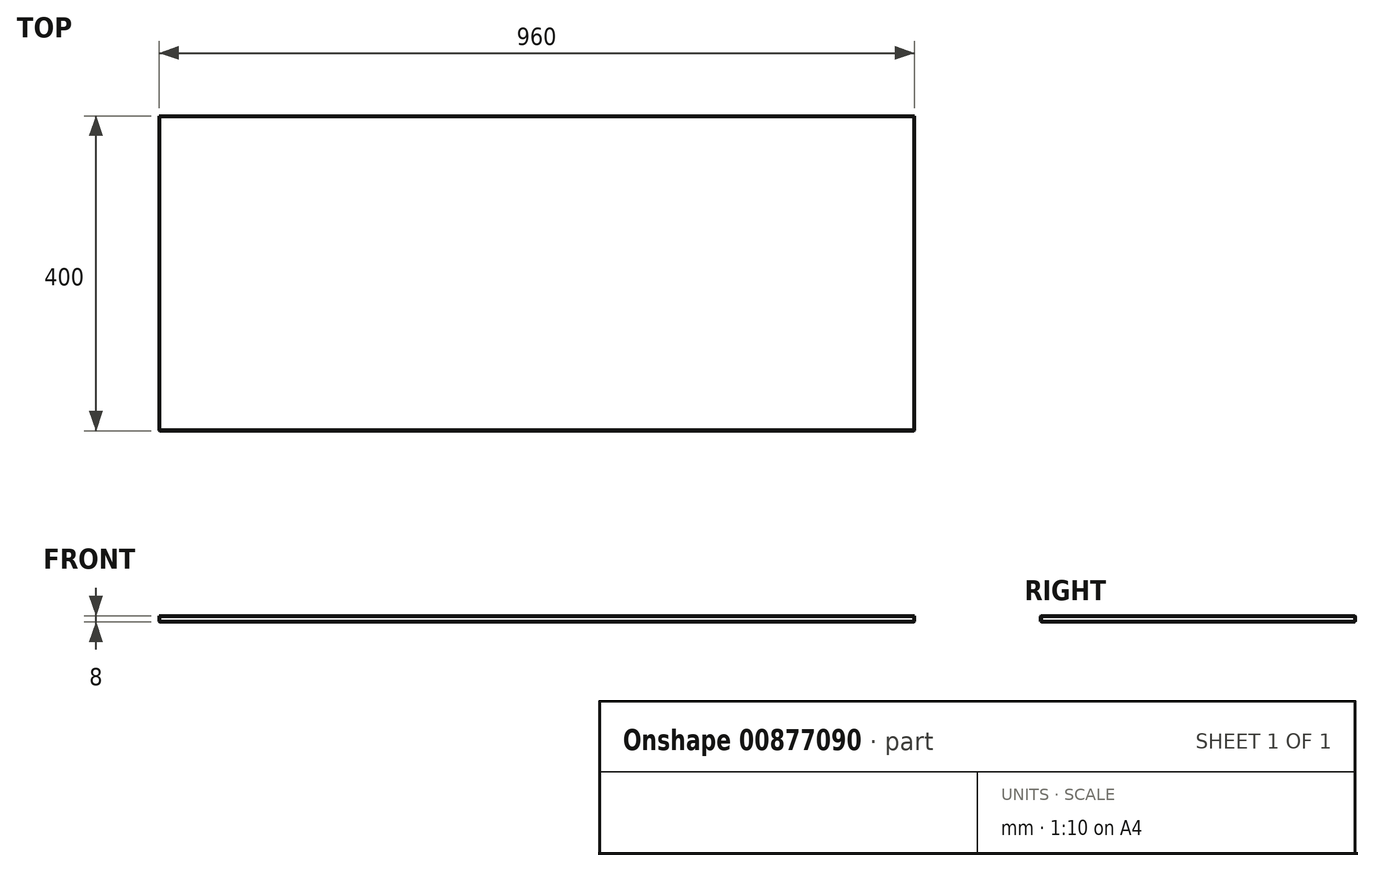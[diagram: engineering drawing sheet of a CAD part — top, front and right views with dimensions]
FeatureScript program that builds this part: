
annotation { "Feature Type Name" : "Feature", "Feature Type Description" : "" }
export const myFeature = defineFeature(function(context is Context, id is Id, definition is map)
    precondition{}
    {
        {
            var Q0;
            Q0=qCreatedBy(makeId("Top.planeOp"),FACE);
            var sketch = newSketch(context, id + "F0", { "sketchPlane" : qUnion([Q0])});
            skLineSegment(sketch, "E0.bottom", {"start": v(-480, 200) * mm, "end": v(480, 200) * mm});
            skLineSegment(sketch, "E0.top", {"start": v(-480, -200) * mm, "end": v(480, -200) * mm});
            skLineSegment(sketch, "E0.left", {"start": v(-480, 200) * mm, "end": v(-480, -200) * mm});
            skLineSegment(sketch, "E0.right", {"start": v(480, 200) * mm, "end": v(480, -200) * mm});
            skPoint(sketch, "E0.middle", {"position": v(0, 0) * mm});
            skSolve(sketch);
        }
        {
            var Q0;
            Q0=makeQuery(id+"F0.imprint","IMPRINT",FACE,{"disambiguationData":[TD([[makeQuery(id+"F0.imprint","IMPRINT",EDGE,{"derivedFrom":sQuery(id+"F0.wireOp",EDGE,"E0.bottom")}),-1.0]])]});
            extrude(context, id + "F1", {"entities" : qUnion([Q0]), "endBound" : BoundingType.SYMMETRIC, "depth" : 8 * mm, "offsetDistance" : 25 * mm});
        }
        {
            var Q0;
            Q0=makeQuery(id+"F1.opExtrude","CAP_EDGE",EDGE,{"disambiguationData":[OSD([sQuery(id+"F0.wireOp",EDGE,"E0.top")])],"isStart":false});
            chamfer(context, id + "F2", {"entities" : qUnion([Q0]), "width" : 1 * mm, "tangentPropagation" : true});
        }
        {
            var Q0;
            Q0=makeQuery(id+"F1.opExtrude","CAP_EDGE",EDGE,{"disambiguationData":[OSD([sQuery(id+"F0.wireOp",EDGE,"E0.right")])],"isStart":false});
            chamfer(context, id + "F3", {"entities" : qUnion([Q0]), "width" : 1 * mm, "tangentPropagation" : true});
        }
        {
            var Q0;
            Q0=makeQuery(id+"F1.opExtrude","CAP_EDGE",EDGE,{"disambiguationData":[OSD([sQuery(id+"F0.wireOp",EDGE,"E0.bottom")])],"isStart":false});
            chamfer(context, id + "F4", {"entities" : qUnion([Q0]), "width" : 1 * mm, "tangentPropagation" : true});
        }
        {
            var Q0;
            Q0=makeQuery(id+"F1.opExtrude","CAP_EDGE",EDGE,{"disambiguationData":[OSD([sQuery(id+"F0.wireOp",EDGE,"E0.top")])],"isStart":true});
            var Q1;
            Q1=makeQuery(id+"F1.opExtrude","CAP_EDGE",EDGE,{"disambiguationData":[OSD([sQuery(id+"F0.wireOp",EDGE,"E0.left")])],"isStart":true});
            var Q2;
            Q2=makeQuery(id+"F1.opExtrude","CAP_EDGE",EDGE,{"disambiguationData":[OSD([sQuery(id+"F0.wireOp",EDGE,"E0.bottom")])],"isStart":true});
            var Q3;
            Q3=makeQuery(id+"F1.opExtrude","CAP_EDGE",EDGE,{"disambiguationData":[OSD([sQuery(id+"F0.wireOp",EDGE,"E0.right")])],"isStart":true});
            chamfer(context, id + "F5", {"entities" : qUnion([Q0, Q1, Q2, Q3]), "width" : 1 * mm, "tangentPropagation" : true});
        }
        {
            var Q0;
            Q0=makeQuery(id+"F1.opExtrude","CAP_EDGE",EDGE,{"disambiguationData":[OSD([sQuery(id+"F0.wireOp",EDGE,"E0.left")])],"isStart":false});
            chamfer(context, id + "F6", {"entities" : qUnion([Q0]), "width" : 1 * mm, "tangentPropagation" : true});
        }
        {
            var Q0;
            Q0=makeQuery(id+"F1.opExtrude","SWEPT_EDGE",EDGE,{"disambiguationData":[OSD([sQuery(id+"F0.wireOp",EDGE,"E0.bottom"),sQuery(id+"F0.wireOp",EDGE,"E0.left")])]});
            chamfer(context, id + "F7", {"entities" : qUnion([Q0]), "width" : 1 * mm, "tangentPropagation" : true});
        }
        {
            var Q0;
            Q0=makeQuery(id+"F1.opExtrude","SWEPT_EDGE",EDGE,{"disambiguationData":[OSD([sQuery(id+"F0.wireOp",EDGE,"E0.top"),sQuery(id+"F0.wireOp",EDGE,"E0.left")])]});
            chamfer(context, id + "F8", {"entities" : qUnion([Q0]), "width" : 1 * mm, "tangentPropagation" : true});
        }
        {
            var Q0;
            Q0=makeQuery(id+"F1.opExtrude","SWEPT_EDGE",EDGE,{"disambiguationData":[OSD([sQuery(id+"F0.wireOp",EDGE,"E0.top"),sQuery(id+"F0.wireOp",EDGE,"E0.right")])]});
            chamfer(context, id + "F9", {"entities" : qUnion([Q0]), "width" : 1 * mm, "tangentPropagation" : true});
        }
        {
            var Q0;
            Q0=makeQuery(id+"F1.opExtrude","SWEPT_EDGE",EDGE,{"disambiguationData":[OSD([sQuery(id+"F0.wireOp",EDGE,"E0.bottom"),sQuery(id+"F0.wireOp",EDGE,"E0.right")])]});
            chamfer(context, id + "F10", {"entities" : qUnion([Q0]), "width" : 1 * mm, "tangentPropagation" : true});
        }
    });
